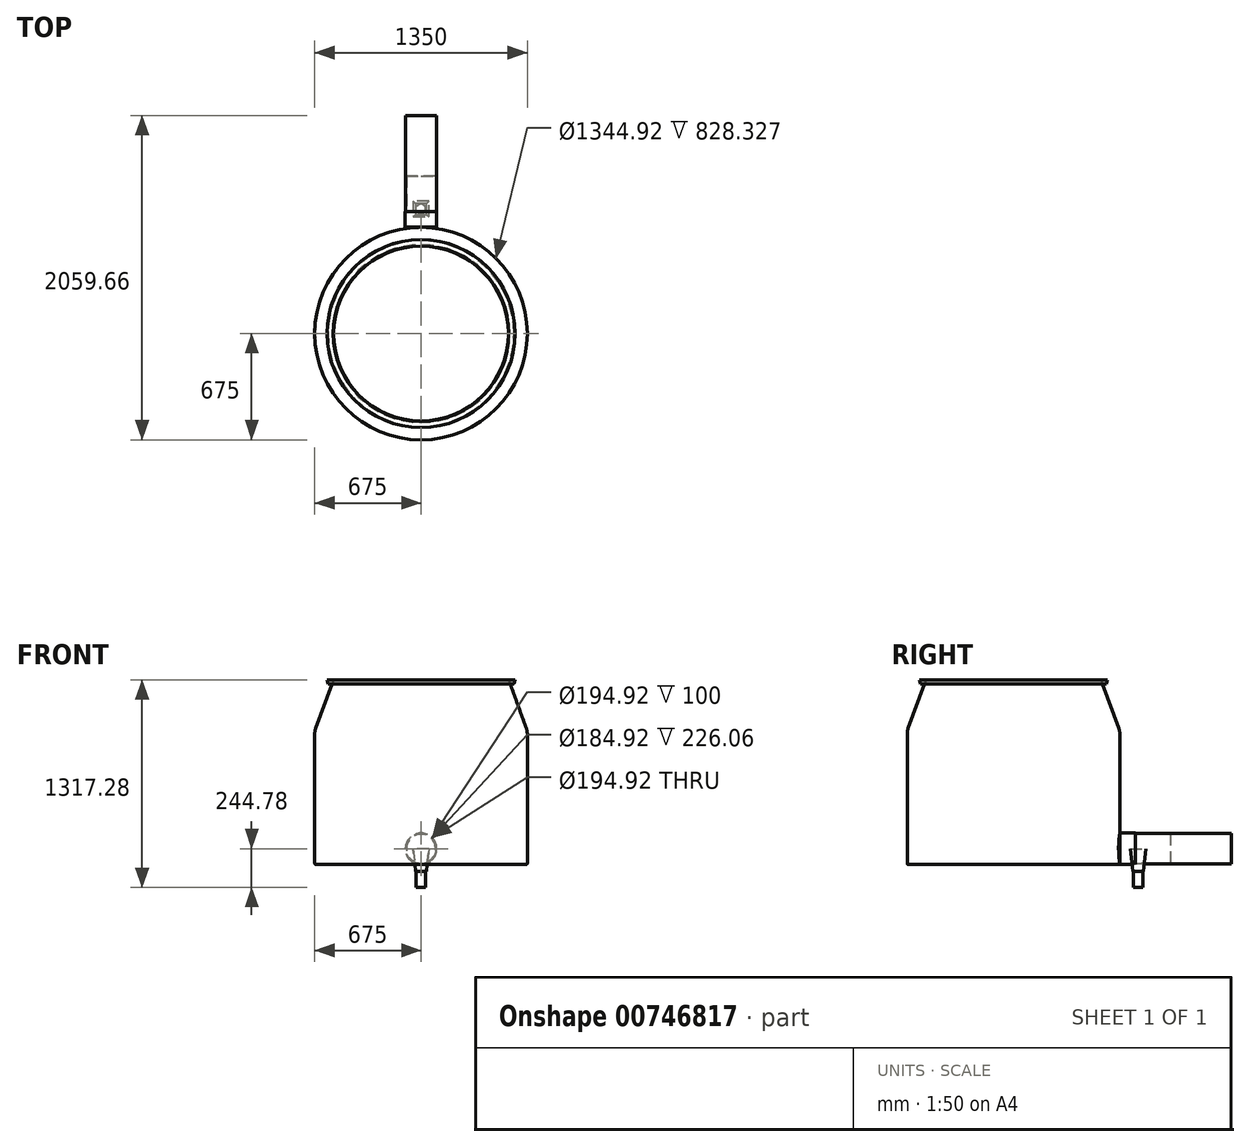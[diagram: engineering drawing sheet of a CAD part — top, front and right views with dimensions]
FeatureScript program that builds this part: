
annotation { "Feature Type Name" : "Feature", "Feature Type Description" : "" }
export const myFeature = defineFeature(function(context is Context, id is Id, definition is map)
    precondition{}
    {
        {
            var Q0;
            Q0=qCreatedBy(makeId("Top.planeOp"),FACE);
            var sketch = newSketch(context, id + "F0", { "sketchPlane" : qUnion([Q0])});
            skCircle(sketch, "E0", {"center": v(0, 0) * mm, "radius": 675 * mm});
            skSolve(sketch);
        }
        {
            var Q0;
            Q0=qSketchRegion(id+"F0",true);
            extrude(context, id + "F1", {"entities" : qUnion([Q0]), "depth" : 848.5 * mm, "offsetDistance" : 25.4 * mm});
        }
        {
            var Q0;
            Q0=makeQuery(id+"F1.opExtrude","CAP_FACE",FACE,{"disambiguationData":[OSD([sQuery(id+"F0.wireOp",EDGE,"E0")])],"isStart":false});
            var sketch = newSketch(context, id + "F2", { "sketchPlane" : qUnion([Q0])});
            skCircle(sketch, "E1", {"center": v(0, 0) * mm, "radius": 675 * mm});
            skSolve(sketch);
        }
        {
            var Q0;
            Q0=qSketchRegion(id+"F2",true);
            extrude(context, id + "F3", {"entities" : qUnion([Q0]), "operationType" : NewBodyOperationType.ADD, "depth" : 424 * mm - 100 * mm, "offsetDistance" : 25.4 * mm, "hasDraft" : true, "draftAngle" : 20 * degree, "draftPullDirection" : true});
        }
        {
            var Q0;
            Q0=makeQuery(id+"F3.boolean.opBoolean","MERGE",EDGE,{"derivedFrom":[makeQuery(id+"F1.opExtrude","CAP_EDGE",EDGE,{"disambiguationData":[OSD([sQuery(id+"F0.wireOp",EDGE,"E0")])],"isStart":false}),makeQuery(id+"F3.opExtrude","CAP_EDGE",EDGE,{"disambiguationData":[OSD([sQuery(id+"F2.wireOp",EDGE,"E1")])],"isStart":true})]});
            fillet(context, id + "F4", {"entities" : qUnion([Q0]), "radius" : 100 * mm, "tangentPropagation" : true, "allowEdgeOverflow" : false});
        }
        {
            var Q0;
            Q0=makeQuery(id+"F3.opExtrude","CAP_FACE",FACE,{"disambiguationData":[OSD([sQuery(id+"F2.wireOp",EDGE,"E1")])],"isStart":false});
            shell(context, id + "F5", {"entities" : qUnion([Q0]), "thickness" : 2.54 * mm});
        }
        {
            var Q0;
            Q0=makeQuery(id+"F3.opExtrude","CAP_FACE",FACE,{"disambiguationData":[OSD([sQuery(id+"F2.wireOp",EDGE,"E1")])],"isStart":false});
            var sketch = newSketch(context, id + "F6", { "sketchPlane" : qUnion([Q0])});
            skCircle(sketch, "E2", {"center": v(0, 0) * mm, "radius": 597.07 * mm});
            skSolve(sketch);
        }
        {
            var Q0;
            Q0=makeQuery(id+"F6.imprint","IMPRINT",FACE,{"disambiguationData":[TD([[makeQuery(id+"F6.imprint","IMPRINT",EDGE,{"derivedFrom":sQuery(id+"F6.wireOp",EDGE,"E2")}),1.0]])]});
            extrude(context, id + "F7", {"entities" : qUnion([Q0]), "oppositeDirection" : true, "depth" : 25.4 * mm, "offsetDistance" : 25.4 * mm, "hasDraft" : true, "draftAngle" : 15 * degree, "draftPullDirection" : true});
        }
        {
            var Q0;
            Q0=makeQuery(id+"F1.opExtrude","CAP_EDGE",EDGE,{"disambiguationData":[OSD([sQuery(id+"F0.wireOp",EDGE,"E0")])],"isStart":true});
            fillet(context, id + "F8", {"entities" : qUnion([Q0]), "radius" : 8 * mm, "tangentPropagation" : true, "allowEdgeOverflow" : false});
        }
        {
            var Q0;
            Q0=makeQuery(id+"F3.opExtrude","SWEPT_FACE",FACE,{"disambiguationData":[OSD([sQuery(id+"F2.wireOp",EDGE,"E1")])]});
            fillet(context, id + "F9", {"entities" : qUnion([Q0]), "radius" : 8 * mm, "tangentPropagation" : true, "allowEdgeOverflow" : false});
        }
        {
            var Q0;
            Q0=qCreatedBy(makeId("Front.planeOp"),FACE);
            cPlane(context, id + "F10", {"entities" : qUnion([Q0]), "cplaneType" : CPlaneType.OFFSET, "offset" : 675.06 * mm, "oppositeDirection" : true, "width" : 152.4 * mm, "height" : 152.4 * mm});
        }
        {
            var Q0;
            Q0=qCreatedBy(id+"F10.planeOp",FACE);
            var sketch = newSketch(context, id + "F11", { "sketchPlane" : qUnion([Q0])});
            skCircle(sketch, "E3", {"center": v(0, 100) * mm, "radius": 100 * mm});
            skSolve(sketch);
        }
        {
            var Q0;
            Q0=qSketchRegion(id+"F11",true);
            extrude(context, id + "F12", {"entities" : qUnion([Q0]), "oppositeDirection" : true, "depth" : 100 * mm, "offsetDistance" : 25.4 * mm});
        }
        {
            var Q0;
            Q0=makeQuery(id+"F12.opExtrude","CAP_FACE",FACE,{"disambiguationData":[OSD([sQuery(id+"F11.wireOp",EDGE,"E3")])],"isStart":false});
            shell(context, id + "F13", {"entities" : qUnion([Q0]), "thickness" : 2.54 * mm});
        }
        {
            var Q0;
            {var subQ0=sQuery(id+"F11.wireOp",EDGE,"E3");Q0=makeQuery(id+"F13.opShell","OFFSET_FACE",FACE,{"disambiguationData":[OSD([subQ0]),TDD([makeQuery(id+"F12.opExtrude","CAP_FACE",FACE,{"disambiguationData":[OSD([subQ0])],"isStart":true})])]});}
            extrude(context, id + "F14", {"entities" : qUnion([Q0]), "operationType" : NewBodyOperationType.REMOVE, "oppositeDirection" : true, "depth" : 416.56 * mm, "offsetDistance" : 25.4 * mm});
        }
        {
            var Q0;
            Q0=qCreatedBy(id+"F10.planeOp",FACE);
            var sketch = newSketch(context, id + "F15", { "sketchPlane" : qUnion([Q0])});
            skCircle(sketch, "E4", {"center": v(0, 100) * mm, "radius": 97.46 * mm});
            skSolve(sketch);
        }
        {
            var Q0;
            Q0=qSketchRegion(id+"F15",true);
            extrude(context, id + "F16", {"entities" : qUnion([Q0]), "operationType" : NewBodyOperationType.REMOVE, "depth" : 80.52 * mm, "offsetDistance" : 25.4 * mm});
        }
        {
            var Q0;
            Q0=makeQuery(id+"F12.opExtrude","CAP_FACE",FACE,{"disambiguationData":[OSD([sQuery(id+"F11.wireOp",EDGE,"E3")])],"isStart":false});
            var sketch = newSketch(context, id + "F17", { "sketchPlane" : qUnion([Q0])});
            skCircle(sketch, "E5", {"center": v(0, 100) * mm, "radius": 97.46 * mm});
            skSolve(sketch);
        }
        {
            var Q0;
            Q0=qSketchRegion(id+"F17",true);
            extrude(context, id + "F18", {"entities" : qUnion([Q0]), "depth" : 609.6 * mm, "offsetDistance" : 25.4 * mm});
        }
        {
            var Q0;
            Q0=makeQuery(id+"F18.opExtrude","CAP_FACE",FACE,{"disambiguationData":[OSD([sQuery(id+"F17.wireOp",EDGE,"E5")])],"isStart":true});
            var sketch = newSketch(context, id + "F19", { "sketchPlane" : qUnion([Q0])});
            skCircle(sketch, "E6", {"center": v(0, 100) * mm, "radius": 92.46 * mm});
            skSolve(sketch);
        }
        {
            var Q0;
            Q0=qSketchRegion(id+"F19",true);
            extrude(context, id + "F20", {"entities" : qUnion([Q0]), "operationType" : NewBodyOperationType.REMOVE, "oppositeDirection" : true, "depth" : 226.06 * mm, "offsetDistance" : 25.4 * mm});
        }
        {
            var Q0;
            Q0=makeQuery(id+"F12.opExtrude","CAP_EDGE",EDGE,{"disambiguationData":[OSD([sQuery(id+"F11.wireOp",EDGE,"E3")])],"isStart":false});
            cPlane(context, id + "F21", {"entities" : qUnion([Q0]), "cplaneType" : CPlaneType.LINE_ANGLE, "offset" : 25.4 * mm, "angle" : 0 * degree, "width" : 152.4 * mm, "height" : 152.4 * mm});
        }
        {
            var Q0;
            Q0=qCreatedBy(id+"F21.planeOp",FACE);
            var sketch = newSketch(context, id + "F22", { "sketchPlane" : qUnion([Q0])});
            skLineSegment(sketch, "E7.bottom", {"start": v(50, -841.78) * mm, "end": v(-50, -841.78) * mm});
            skLineSegment(sketch, "E7.top", {"start": v(50, -741.78) * mm, "end": v(-50, -741.78) * mm});
            skLineSegment(sketch, "E7.left", {"start": v(50, -841.78) * mm, "end": v(50, -741.78) * mm});
            skLineSegment(sketch, "E7.right", {"start": v(-50, -841.78) * mm, "end": v(-50, -741.78) * mm});
            skLineSegment(sketch, "E8", {"start": v(0, -968.1) * mm, "end": v(0, -610.36) * mm, "construction": true});
            skSolve(sketch);
        }
        {
            var Q0;
            Q0 = qSketchRegion(id + "F22", true);
            extrude(context, id + "F23", {"entities" : qUnion([Q0]), "depth" : 144.78 * mm, "offsetDistance" : 25.4 * mm, "hasDraft" : true, "draftAngle" : 6 * degree, "draftPullDirection" : true});
        }
        {
            var Q0;
            Q0=makeQuery(id+"F23.opExtrude","CAP_FACE",FACE,{"disambiguationData":[OSD([sQuery(id+"F22.wireOp",EDGE,"E7.bottom"),sQuery(id+"F22.wireOp",EDGE,"E7.top"),sQuery(id+"F22.wireOp",EDGE,"E7.left"),sQuery(id+"F22.wireOp",EDGE,"E7.right")])],"isStart":false});
            var sketch = newSketch(context, id + "F24", { "sketchPlane" : qUnion([Q0])});
            skCircle(sketch, "E9", {"center": v(0, -791.78) * mm, "radius": 30 * mm});
            skLineSegment(sketch, "E10", {"start": v(122.93, -791.78) * mm, "end": v(-110.02, -791.78) * mm, "construction": true});
            skLineSegment(sketch, "E11", {"start": v(0, -943.72) * mm, "end": v(0, -740.33) * mm, "construction": true});
            skLineSegment(sketch, "E12", {"start": v(-34.78, -826.57) * mm, "end": v(-34.78, -801.07) * mm});
            skLineSegment(sketch, "E13", {"start": v(-34.78, -826.57) * mm, "end": v(-11.46, -826.57) * mm});
            skArc(sketch, "E14", {"start": v(-34.78, -801.07) * mm, "mid": v(-25.24, -815.76) * mm, "end": v(-11.46, -826.57) * mm});
            skLineSegment(sketch, "E15", {"start": v(34.78, -826.57) * mm, "end": v(34.78, -801.26) * mm});
            skLineSegment(sketch, "E16", {"start": v(34.78, -826.57) * mm, "end": v(9.48, -826.57) * mm});
            skArc(sketch, "E17", {"start": v(9.48, -826.57) * mm, "mid": v(24.47, -816.26) * mm, "end": v(34.78, -801.26) * mm});
            skLineSegment(sketch, "E18", {"start": v(34.78, -757) * mm, "end": v(12.02, -757) * mm});
            skLineSegment(sketch, "E19", {"start": v(34.78, -757) * mm, "end": v(34.78, -780.55) * mm});
            skArc(sketch, "E20", {"start": v(34.78, -780.55) * mm, "mid": v(25.2, -767.03) * mm, "end": v(12.02, -757) * mm});
            skLineSegment(sketch, "E21", {"start": v(-34.78, -757) * mm, "end": v(-34.78, -781.85) * mm});
            skLineSegment(sketch, "E22", {"start": v(-34.78, -757) * mm, "end": v(-11.55, -757) * mm});
            skArc(sketch, "E23", {"start": v(-11.55, -757) * mm, "mid": v(-25.28, -767.45) * mm, "end": v(-34.78, -781.85) * mm});
            skSolve(sketch);
        }
        {
            var Q0;
            {var subQ0=sQuery(id+"F24.wireOp",EDGE,"E9");var subQ1=makeQuery(id+"F24.imprint","INTERSECT",VERTEX,{"derivedFrom":[makeQuery(id+"F23.opExtrude","CAP_EDGE",EDGE,{"disambiguationData":[OSD([sQuery(id+"F22.wireOp",EDGE,"E7.top")])],"isStart":false}),subQ0]});Q0=makeQuery(id+"F24.imprint","IMPRINT",FACE,{"disambiguationData":[TD([[makeQuery(id+"F24.imprint","IMPRINT",EDGE,{"disambiguationData":[TD([[subQ1,1.0]])],"derivedFrom":subQ0}),1.0]])]});}
            extrude(context, id + "F25", {"entities" : qUnion([Q0]), "operationType" : NewBodyOperationType.ADD, "depth" : 100 * mm, "offsetDistance" : 25.4 * mm});
        }
    });
